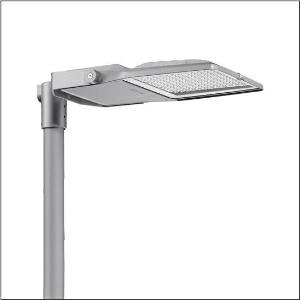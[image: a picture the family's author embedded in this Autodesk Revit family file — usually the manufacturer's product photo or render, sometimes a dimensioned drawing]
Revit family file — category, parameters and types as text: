
# Revit family: floodlight_fl_21_iq_midi___pl33t_5xa7781f2f3a_a5b2
name_source: partatom
category: Lighting Fixtures
units: mm (PartAtom-declared; Revit-internal decimal feet)

## family parameters
Cut with Voids When Loaded = No
Host = Face
Light Source = No
Part Type = Normal
Room Calculation Point = No
Round Connector Dimension = Use Diameter
Shared = No

## types (1)
- --- (1 x LED, 35350 lm, 270.2 W, 3000K)
    Apparent Load = 270 VA
    CIE Flux Codes = 26 75 99 100 100
    Color Rendering = 70
    Color Temperature = 3000K
    Default Elevation = 1800 mm
    Description = Floodlight FL 21 iQ midi, floodlight, primary light control with lens, of PMMA, primary optical cover: protective disc, of toughened safety glass, transparent, light distribution: PL33T, light emission: direct distribution, installation type: surface-mounted, LED, High Power LED, rated luminous flux: 35.350lm, luminous efficacy: 131lm/W, light colour: 730, colour temperature: 3000K, control gear: ECG iQ, control: optimised constant luminous flux control (CLO 2.0), Desk-Remote (wireless, voltage-free reading and setting of iQ features in the workshop via application-optimized NFC function/RFID function), Light-Fading, Smart-Wire, Night-Set, Lumen-Switch, Temp-Guard, Auto-Match, with terminal, 6-pole, mains connection: 220..240V, AC, 50/60Hz, start of lifetime: 270W, end of service life: 287W, reduction: 117W, luminaire housing, of diecast aluminium, powder-coated, Siteco® metallic grey (DB 702S), corrosivity category C5 mid according to DIN EN ISO 12944, sealing non-destructively replaceable, please order mast flange separately, mast bracket, of steel, galvanised, powder-coated, Siteco® metallic grey (DB 702S), protection rating (complete): IP66, insulation class (complete): insulation class II (safety insulation), certification: CE, protection symbol: D, impact resistance: IK08, permissible operating ambient temperature: -40..+40°C, permissible operating ambient temperature for outdoor applications: -40..+50°C, standard: DIN EN 12944, LABS conformity tested according to VDMA 24364:2018-05, packaging unit: 1 piece

Light Distribution: PL33T
    Height = 76 mm
    Lamp = 1 x LED
    Lamp Light Flux = 35350 lm
    Lamp Power = 270.2 W
    Lamp count = 1
    Length = 657 mm
    Luminous efficacy = 131 lm/W
    Manufacturer = Siteco
    ModVariant = No
    Model = 5XA7781F2F3A
    Number of Poles = 1
    OnlyDefault = Yes
    Power Factor = 1
    Product Name = Floodlight FL 21 iQ midi | PL33T
    Product group = floodlight | pylon annexe
    ProductGroupID = 6200
    Protection Class = Protection class II
    Protection Degree = IP 66
    RLX_Detail_Level = 1
    RLX_Emergency_Light_Flux = 0 lm
    RLX_Emergency_Type = 0
    RLX_Emergency_Type_DB = No
    RlxData = <blob elided: 153729 chars, md5=84d1ad71>
    Socket = socket
    Standby Power = 0 W
    System Light Flux = 35350 lm
    System Power = 270 W
    Type Comments = factory setting: luminous flux: 100 % | dim-lin: 254 | 620 mA
    Type Image = l_1007123.jpg
    URL = http://relux.com
    VarID = @adj_051849
    Voltage = 0 V
    Weight = 0.00 kg
    Width = 442 mm

## geometry (parser evidence)
native form markers: Blend x4, Sweep x13
no freeform markers — native parametric forms only
